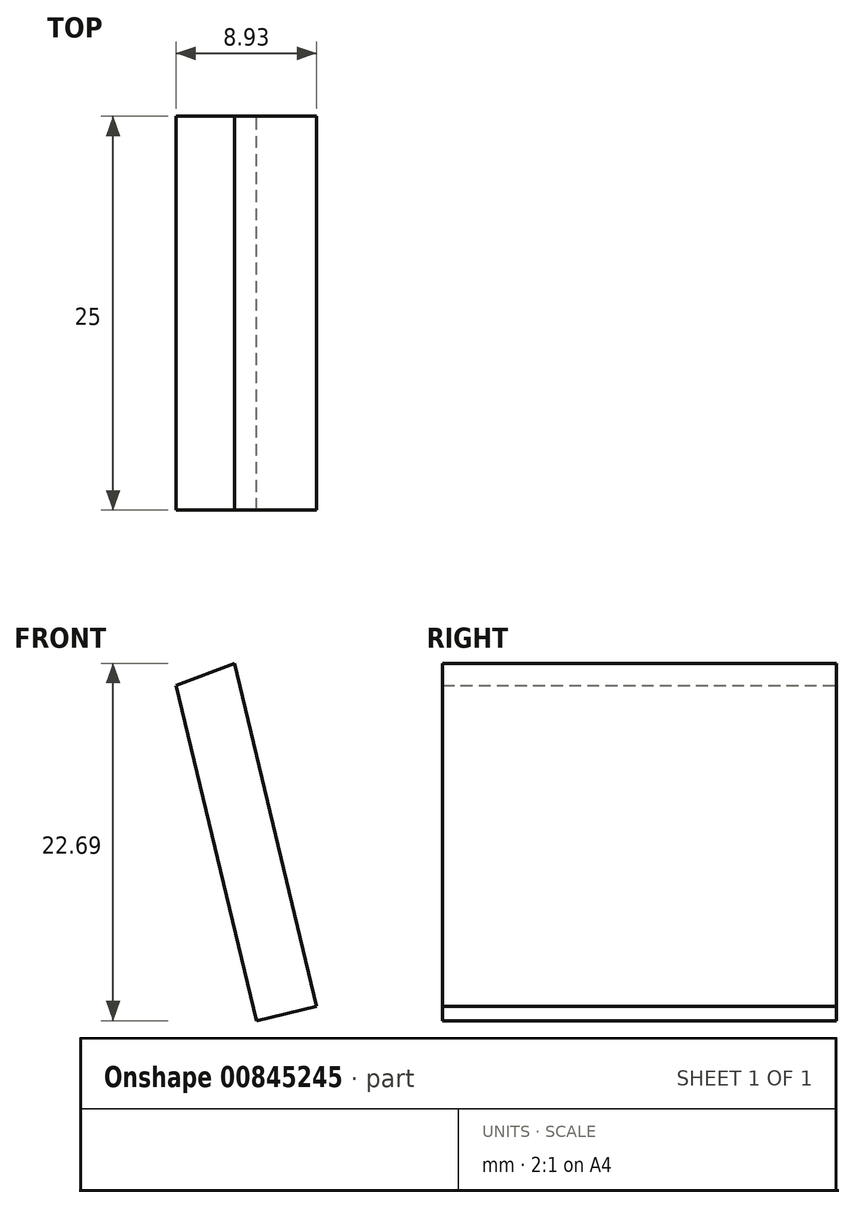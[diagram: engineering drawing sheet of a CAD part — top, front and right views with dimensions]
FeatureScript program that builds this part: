
annotation { "Feature Type Name" : "Feature", "Feature Type Description" : "" }
export const myFeature = defineFeature(function(context is Context, id is Id, definition is map)
    precondition{}
    {
        {
            var Q0;
            Q0=qCreatedBy(makeId("Front.planeOp"),FACE);
            var sketch = newSketch(context, id + "F0", { "sketchPlane" : qUnion([Q0])});
            skLineSegment(sketch, "E0", {"start": v(64.43, 13.8) * mm, "end": v(69.53, -7.5) * mm});
            skLineSegment(sketch, "E1", {"start": v(69.53, -7.5) * mm, "end": v(73.36, -6.58) * mm});
            skLineSegment(sketch, "E2", {"start": v(73.36, -6.58) * mm, "end": v(68.14, 15.19) * mm});
            skLineSegment(sketch, "E3", {"start": v(68.14, 15.19) * mm, "end": v(64.43, 13.8) * mm});
            skSolve(sketch);
        }
        {
            var Q0;
            Q0=makeQuery(id+"F0.imprint","IMPRINT",FACE,{"disambiguationData":[TD([[makeQuery(id+"F0.imprint","IMPRINT",EDGE,{"derivedFrom":sQuery(id+"F0.wireOp",EDGE,"E0")}),1.0]])]});
            extrude(context, id + "F1", {"entities" : qUnion([Q0]), "depth" : 25 * mm, "offsetDistance" : 25 * mm});
        }
    });
